# Revit family: RKB 800X500 B3 ErP AC_7480165
name_source: partatom
category: Mechanical Equipment
revit_build: Autodesk Revit MEP 2014 (Build: 20130308_1515(x64)
units: mm (PartAtom-declared; Revit-internal decimal feet)

## types (1)
- RKB 800X500 B3 ErP AC
    Capacitor = - μF
    Connector Height = 500 mm  [stored 1.64042 ft]
    Connector Width = 800 mm  [stored 2.62467 ft]
    Current = 1 A
    Depth = 843 mm  [stored 2.76575 ft]
    Description = UNINSULATED DUCT FANS WITH RECTANGULAR CONNECTIONS
    Frequency = 50 Hz
    Height = 557 mm  [stored 1.82743 ft]
    Main Material = Steel, Galvanized
    Max. temperature of transported air = 60 °C
    Max. temperature of transported air when speed controlled = 60 °C
    Phase = 3
    Power = 639 W
    Sound pressure level at 3 m = 54 dB(A)
    Speed = 880 rpm
    Voltage = 400 V
    Voltage range = 380-418 V
    Weight = 61.80 kg
    Width = 913 mm
    Wiring diagram = Y 4040004 / Δ4040003

note: [stored X ft] marks values corroborated as IEEE doubles in the binary element streams (Revit-internal decimal feet)

## geometry (parser evidence)
native form markers: Sweep x4
no freeform markers — native parametric forms only
